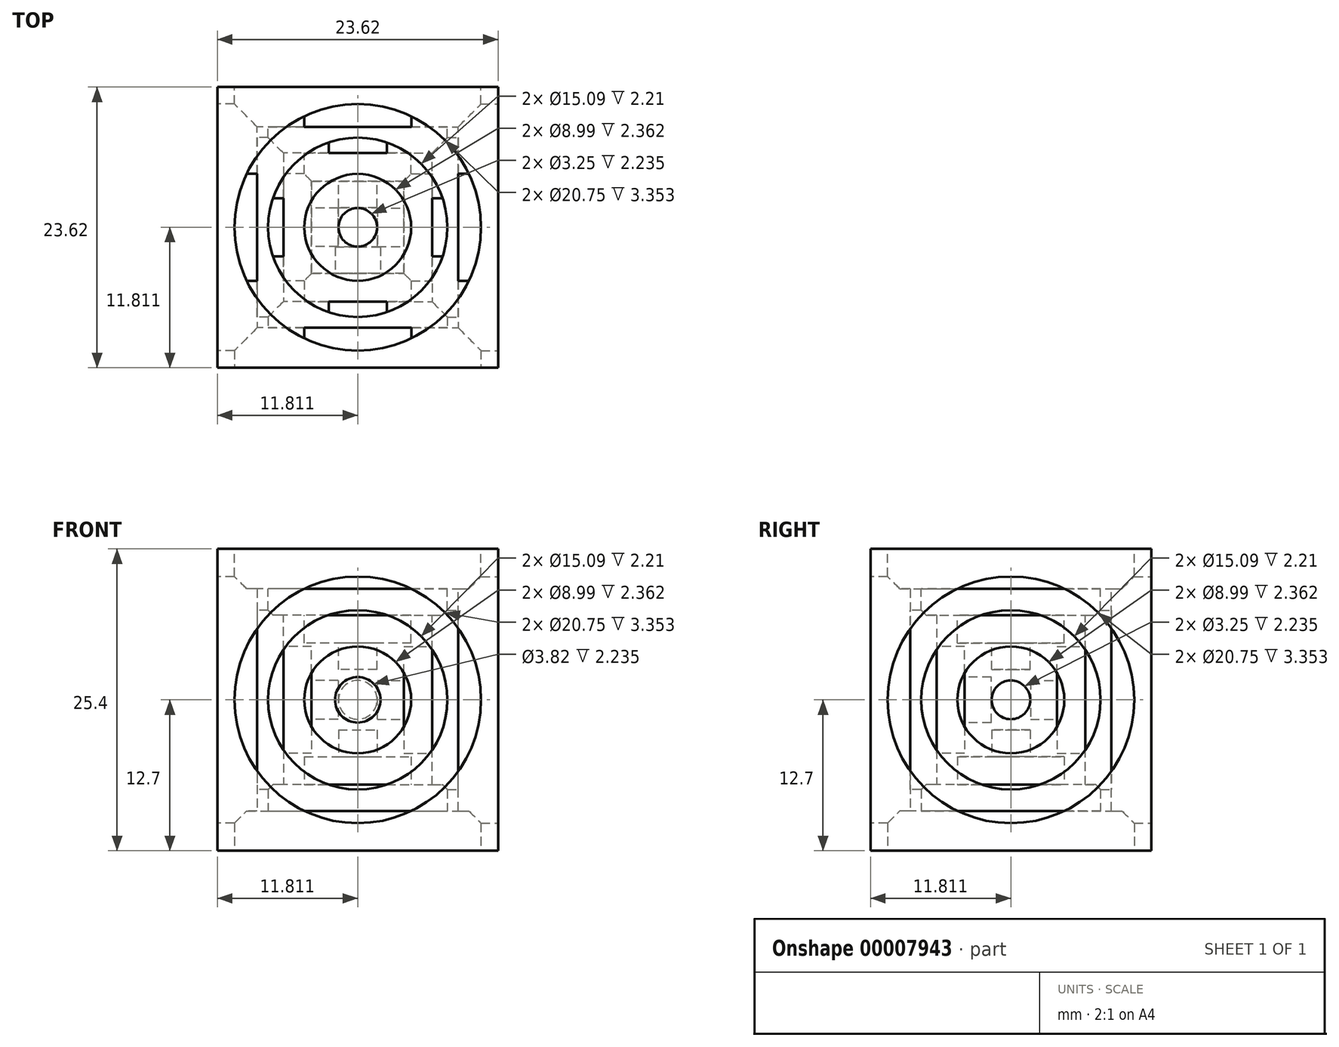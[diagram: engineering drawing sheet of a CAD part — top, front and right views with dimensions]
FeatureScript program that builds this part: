
annotation { "Feature Type Name" : "Feature", "Feature Type Description" : "" }
export const myFeature = defineFeature(function(context is Context, id is Id, definition is map)
    precondition{}
    {
        {
            var Q0;
            Q0=qCreatedBy(makeId("Top.planeOp"),FACE);
            var sketch = newSketch(context, id + "F0", { "sketchPlane" : qUnion([Q0])});
            skLineSegment(sketch, "E0.bottom", {"start": v(0, 0) * mm, "end": v(23.62, 0) * mm});
            skLineSegment(sketch, "E0.top", {"start": v(0, 23.62) * mm, "end": v(23.62, 23.62) * mm});
            skLineSegment(sketch, "E0.left", {"start": v(0, 0) * mm, "end": v(0, 23.62) * mm});
            skLineSegment(sketch, "E0.right", {"start": v(23.62, 0) * mm, "end": v(23.62, 23.62) * mm});
            skSolve(sketch);
        }
        {
            var Q0;
            Q0=makeQuery(id+"F0.imprint","IMPRINT",FACE,{"disambiguationData":[TD([[makeQuery(id+"F0.imprint","IMPRINT",EDGE,{"derivedFrom":sQuery(id+"F0.wireOp",EDGE,"E0.bottom")}),1.0]])]});
            extrude(context, id + "F1", {"entities" : qUnion([Q0]), "depth" : 25.4 * mm});
        }
        {
            var Q0;
            Q0=makeQuery(id+"F1.opExtrude","CAP_FACE",FACE,{"disambiguationData":[OSD([sQuery(id+"F0.wireOp",EDGE,"E0.bottom"),sQuery(id+"F0.wireOp",EDGE,"E0.top"),sQuery(id+"F0.wireOp",EDGE,"E0.left"),sQuery(id+"F0.wireOp",EDGE,"E0.right")])],"isStart":false});
            var sketch = newSketch(context, id + "F2", { "sketchPlane" : qUnion([Q0])});
            skCircle(sketch, "E1", {"center": v(11.81, 11.81) * mm, "radius": 1.63 * mm});
            skSolve(sketch);
        }
        {
            var Q0;
            Q0=makeQuery(id+"F2.imprint","IMPRINT",FACE,{"disambiguationData":[TD([[makeQuery(id+"F2.imprint","IMPRINT",EDGE,{"derivedFrom":sQuery(id+"F2.wireOp",EDGE,"E1")}),1.0]])]});
            extrude(context, id + "F3", {"entities" : qUnion([Q0]), "operationType" : NewBodyOperationType.REMOVE, "oppositeDirection" : true, "depth" : 10.16 * mm});
        }
        {
            var Q0;
            Q0=makeQuery(id+"F1.opExtrude","CAP_FACE",FACE,{"disambiguationData":[OSD([sQuery(id+"F0.wireOp",EDGE,"E0.bottom"),sQuery(id+"F0.wireOp",EDGE,"E0.top"),sQuery(id+"F0.wireOp",EDGE,"E0.left"),sQuery(id+"F0.wireOp",EDGE,"E0.right")])],"isStart":false});
            var sketch = newSketch(context, id + "F4", { "sketchPlane" : qUnion([Q0])});
            skCircle(sketch, "E2", {"center": v(11.81, 11.81) * mm, "radius": 4.5 * mm});
            skSolve(sketch);
        }
        {
            var Q0;
            Q0=makeQuery(id+"F4.imprint","IMPRINT",FACE,{"disambiguationData":[TD([[makeQuery(id+"F4.imprint","IMPRINT",EDGE,{"derivedFrom":sQuery(id+"F4.wireOp",EDGE,"E2")}),1.0]])]});
            extrude(context, id + "F5", {"entities" : qUnion([Q0]), "operationType" : NewBodyOperationType.REMOVE, "oppositeDirection" : true, "depth" : 7.92 * mm});
        }
        {
            var Q0;
            Q0=makeQuery(id+"F1.opExtrude","CAP_FACE",FACE,{"disambiguationData":[OSD([sQuery(id+"F0.wireOp",EDGE,"E0.bottom"),sQuery(id+"F0.wireOp",EDGE,"E0.top"),sQuery(id+"F0.wireOp",EDGE,"E0.left"),sQuery(id+"F0.wireOp",EDGE,"E0.right")])],"isStart":false});
            var sketch = newSketch(context, id + "F6", { "sketchPlane" : qUnion([Q0])});
            skCircle(sketch, "E3", {"center": v(11.81, 11.81) * mm, "radius": 7.54 * mm});
            skSolve(sketch);
        }
        {
            var Q0;
            Q0=makeQuery(id+"F6.imprint","IMPRINT",FACE,{"disambiguationData":[TD([[makeQuery(id+"F6.imprint","IMPRINT",EDGE,{"derivedFrom":sQuery(id+"F6.wireOp",EDGE,"E3")}),1.0]])]});
            extrude(context, id + "F7", {"entities" : qUnion([Q0]), "operationType" : NewBodyOperationType.REMOVE, "oppositeDirection" : true, "depth" : 5.56 * mm});
        }
        {
            var Q0;
            Q0=makeQuery(id+"F1.opExtrude","CAP_FACE",FACE,{"disambiguationData":[OSD([sQuery(id+"F0.wireOp",EDGE,"E0.bottom"),sQuery(id+"F0.wireOp",EDGE,"E0.top"),sQuery(id+"F0.wireOp",EDGE,"E0.left"),sQuery(id+"F0.wireOp",EDGE,"E0.right")])],"isStart":false});
            var sketch = newSketch(context, id + "F8", { "sketchPlane" : qUnion([Q0])});
            skCircle(sketch, "E4", {"center": v(11.81, 11.81) * mm, "radius": 10.38 * mm});
            skSolve(sketch);
        }
        {
            var Q0;
            Q0=makeQuery(id+"F8.imprint","IMPRINT",FACE,{"disambiguationData":[TD([[makeQuery(id+"F8.imprint","IMPRINT",EDGE,{"derivedFrom":sQuery(id+"F8.wireOp",EDGE,"E4")}),1.0]])]});
            extrude(context, id + "F9", {"entities" : qUnion([Q0]), "operationType" : NewBodyOperationType.REMOVE, "oppositeDirection" : true, "depth" : 3.35 * mm});
        }
        {
            var Q0;
            Q0=makeQuery(id+"F1.opExtrude","SWEPT_FACE",FACE,{"disambiguationData":[OSD([sQuery(id+"F0.wireOp",EDGE,"E0.bottom")])]});
            var sketch = newSketch(context, id + "F10", { "sketchPlane" : qUnion([Q0])});
            skCircle(sketch, "E5", {"center": v(11.81, 12.7) * mm, "radius": 1.91 * mm});
            skSolve(sketch);
        }
        {
            var Q0;
            Q0=makeQuery(id+"F10.imprint","IMPRINT",FACE,{"disambiguationData":[TD([[makeQuery(id+"F10.imprint","IMPRINT",EDGE,{"derivedFrom":sQuery(id+"F10.wireOp",EDGE,"E5")}),1.0]])]});
            extrude(context, id + "F11", {"entities" : qUnion([Q0]), "operationType" : NewBodyOperationType.REMOVE, "oppositeDirection" : true, "depth" : 10.16 * mm});
        }
        {
            var Q0;
            Q0=makeQuery(id+"F1.opExtrude","SWEPT_FACE",FACE,{"disambiguationData":[OSD([sQuery(id+"F0.wireOp",EDGE,"E0.bottom")])]});
            var sketch = newSketch(context, id + "F12", { "sketchPlane" : qUnion([Q0])});
            skCircle(sketch, "E6", {"center": v(11.81, 12.7) * mm, "radius": 4.5 * mm});
            skSolve(sketch);
        }
        {
            var Q0;
            Q0=makeQuery(id+"F12.imprint","IMPRINT",FACE,{"disambiguationData":[TD([[makeQuery(id+"F12.imprint","IMPRINT",EDGE,{"derivedFrom":sQuery(id+"F12.wireOp",EDGE,"E6")}),1.0]])]});
            extrude(context, id + "F13", {"entities" : qUnion([Q0]), "operationType" : NewBodyOperationType.REMOVE, "oppositeDirection" : true, "depth" : 7.92 * mm});
        }
        {
            var Q0;
            Q0=makeQuery(id+"F1.opExtrude","SWEPT_FACE",FACE,{"disambiguationData":[OSD([sQuery(id+"F0.wireOp",EDGE,"E0.bottom")])]});
            var sketch = newSketch(context, id + "F14", { "sketchPlane" : qUnion([Q0])});
            skCircle(sketch, "E7", {"center": v(11.81, 12.7) * mm, "radius": 7.54 * mm});
            skSolve(sketch);
        }
        {
            var Q0;
            Q0=makeQuery(id+"F14.imprint","IMPRINT",FACE,{"disambiguationData":[TD([[makeQuery(id+"F14.imprint","IMPRINT",EDGE,{"derivedFrom":sQuery(id+"F14.wireOp",EDGE,"E7")}),1.0]])]});
            extrude(context, id + "F15", {"entities" : qUnion([Q0]), "operationType" : NewBodyOperationType.REMOVE, "oppositeDirection" : true, "depth" : 5.56 * mm});
        }
        {
            var Q0;
            Q0=makeQuery(id+"F1.opExtrude","SWEPT_FACE",FACE,{"disambiguationData":[OSD([sQuery(id+"F0.wireOp",EDGE,"E0.bottom")])]});
            var sketch = newSketch(context, id + "F16", { "sketchPlane" : qUnion([Q0])});
            skCircle(sketch, "E8", {"center": v(11.81, 12.7) * mm, "radius": 10.38 * mm});
            skSolve(sketch);
        }
        {
            var Q0;
            Q0=makeQuery(id+"F16.imprint","IMPRINT",FACE,{"disambiguationData":[TD([[makeQuery(id+"F16.imprint","IMPRINT",EDGE,{"derivedFrom":sQuery(id+"F16.wireOp",EDGE,"E8")}),1.0]])]});
            extrude(context, id + "F17", {"entities" : qUnion([Q0]), "operationType" : NewBodyOperationType.REMOVE, "oppositeDirection" : true, "depth" : 3.35 * mm});
        }
        {
            var Q0;
            Q0=makeQuery(id+"F1.opExtrude","CAP_FACE",FACE,{"disambiguationData":[OSD([sQuery(id+"F0.wireOp",EDGE,"E0.bottom"),sQuery(id+"F0.wireOp",EDGE,"E0.top"),sQuery(id+"F0.wireOp",EDGE,"E0.left"),sQuery(id+"F0.wireOp",EDGE,"E0.right")])],"isStart":true});
            var sketch = newSketch(context, id + "F18", { "sketchPlane" : qUnion([Q0])});
            skCircle(sketch, "E9", {"center": v(11.81, -11.81) * mm, "radius": 1.63 * mm});
            skSolve(sketch);
        }
        {
            var Q0;
            Q0=makeQuery(id+"F18.imprint","IMPRINT",FACE,{"disambiguationData":[TD([[makeQuery(id+"F18.imprint","IMPRINT",EDGE,{"derivedFrom":sQuery(id+"F18.wireOp",EDGE,"E9")}),1.0]])]});
            extrude(context, id + "F19", {"entities" : qUnion([Q0]), "operationType" : NewBodyOperationType.REMOVE, "oppositeDirection" : true, "depth" : 10.16 * mm});
        }
        {
            var Q0;
            Q0=makeQuery(id+"F1.opExtrude","CAP_FACE",FACE,{"disambiguationData":[OSD([sQuery(id+"F0.wireOp",EDGE,"E0.bottom"),sQuery(id+"F0.wireOp",EDGE,"E0.top"),sQuery(id+"F0.wireOp",EDGE,"E0.left"),sQuery(id+"F0.wireOp",EDGE,"E0.right")])],"isStart":true});
            var sketch = newSketch(context, id + "F20", { "sketchPlane" : qUnion([Q0])});
            skCircle(sketch, "E10", {"center": v(11.81, -11.81) * mm, "radius": 4.5 * mm});
            skSolve(sketch);
        }
        {
            var Q0;
            Q0=makeQuery(id+"F20.imprint","IMPRINT",FACE,{"disambiguationData":[TD([[makeQuery(id+"F20.imprint","IMPRINT",EDGE,{"derivedFrom":sQuery(id+"F20.wireOp",EDGE,"E10")}),1.0]])]});
            extrude(context, id + "F21", {"entities" : qUnion([Q0]), "operationType" : NewBodyOperationType.REMOVE, "oppositeDirection" : true, "depth" : 7.92 * mm});
        }
        {
            var Q0;
            Q0=makeQuery(id+"F1.opExtrude","CAP_FACE",FACE,{"disambiguationData":[OSD([sQuery(id+"F0.wireOp",EDGE,"E0.bottom"),sQuery(id+"F0.wireOp",EDGE,"E0.top"),sQuery(id+"F0.wireOp",EDGE,"E0.left"),sQuery(id+"F0.wireOp",EDGE,"E0.right")])],"isStart":true});
            var sketch = newSketch(context, id + "F22", { "sketchPlane" : qUnion([Q0])});
            skCircle(sketch, "E11", {"center": v(11.81, -11.81) * mm, "radius": 7.54 * mm});
            skSolve(sketch);
        }
        {
            var Q0;
            Q0=makeQuery(id+"F22.imprint","IMPRINT",FACE,{"disambiguationData":[TD([[makeQuery(id+"F22.imprint","IMPRINT",EDGE,{"derivedFrom":sQuery(id+"F22.wireOp",EDGE,"E11")}),1.0]])]});
            extrude(context, id + "F23", {"entities" : qUnion([Q0]), "operationType" : NewBodyOperationType.REMOVE, "oppositeDirection" : true, "depth" : 5.56 * mm});
        }
        {
            var Q0;
            Q0=makeQuery(id+"F1.opExtrude","CAP_FACE",FACE,{"disambiguationData":[OSD([sQuery(id+"F0.wireOp",EDGE,"E0.bottom"),sQuery(id+"F0.wireOp",EDGE,"E0.top"),sQuery(id+"F0.wireOp",EDGE,"E0.left"),sQuery(id+"F0.wireOp",EDGE,"E0.right")])],"isStart":true});
            var sketch = newSketch(context, id + "F24", { "sketchPlane" : qUnion([Q0])});
            skCircle(sketch, "E12", {"center": v(11.81, -11.81) * mm, "radius": 10.38 * mm});
            skSolve(sketch);
        }
        {
            var Q0;
            Q0=makeQuery(id+"F24.imprint","IMPRINT",FACE,{"disambiguationData":[TD([[makeQuery(id+"F24.imprint","IMPRINT",EDGE,{"derivedFrom":sQuery(id+"F24.wireOp",EDGE,"E12")}),1.0]])]});
            extrude(context, id + "F25", {"entities" : qUnion([Q0]), "operationType" : NewBodyOperationType.REMOVE, "oppositeDirection" : true, "depth" : 3.35 * mm});
        }
        {
            var Q0;
            Q0=makeQuery(id+"F1.opExtrude","SWEPT_FACE",FACE,{"disambiguationData":[OSD([sQuery(id+"F0.wireOp",EDGE,"E0.right")])]});
            var sketch = newSketch(context, id + "F26", { "sketchPlane" : qUnion([Q0])});
            skCircle(sketch, "E13", {"center": v(11.81, 12.7) * mm, "radius": 1.63 * mm});
            skSolve(sketch);
        }
        {
            var Q0;
            Q0=makeQuery(id+"F26.imprint","IMPRINT",FACE,{"disambiguationData":[TD([[makeQuery(id+"F26.imprint","IMPRINT",EDGE,{"derivedFrom":sQuery(id+"F26.wireOp",EDGE,"E13")}),1.0]])]});
            extrude(context, id + "F27", {"entities" : qUnion([Q0]), "operationType" : NewBodyOperationType.REMOVE, "oppositeDirection" : true, "depth" : 10.16 * mm});
        }
        {
            var Q0;
            Q0=makeQuery(id+"F1.opExtrude","SWEPT_FACE",FACE,{"disambiguationData":[OSD([sQuery(id+"F0.wireOp",EDGE,"E0.right")])]});
            var sketch = newSketch(context, id + "F28", { "sketchPlane" : qUnion([Q0])});
            skCircle(sketch, "E14", {"center": v(11.81, 12.7) * mm, "radius": 4.5 * mm});
            skSolve(sketch);
        }
        {
            var Q0;
            Q0=makeQuery(id+"F28.imprint","IMPRINT",FACE,{"disambiguationData":[TD([[makeQuery(id+"F28.imprint","IMPRINT",EDGE,{"derivedFrom":sQuery(id+"F28.wireOp",EDGE,"E14")}),1.0]])]});
            extrude(context, id + "F29", {"entities" : qUnion([Q0]), "operationType" : NewBodyOperationType.REMOVE, "oppositeDirection" : true, "depth" : 7.92 * mm});
        }
        {
            var Q0;
            Q0=makeQuery(id+"F1.opExtrude","SWEPT_FACE",FACE,{"disambiguationData":[OSD([sQuery(id+"F0.wireOp",EDGE,"E0.right")])]});
            var sketch = newSketch(context, id + "F30", { "sketchPlane" : qUnion([Q0])});
            skCircle(sketch, "E15", {"center": v(11.81, 12.7) * mm, "radius": 7.54 * mm});
            skSolve(sketch);
        }
        {
            var Q0;
            Q0=makeQuery(id+"F30.imprint","IMPRINT",FACE,{"disambiguationData":[TD([[makeQuery(id+"F30.imprint","IMPRINT",EDGE,{"derivedFrom":sQuery(id+"F30.wireOp",EDGE,"E15")}),1.0]])]});
            extrude(context, id + "F31", {"entities" : qUnion([Q0]), "operationType" : NewBodyOperationType.REMOVE, "oppositeDirection" : true, "depth" : 5.56 * mm});
        }
        {
            var Q0;
            Q0=makeQuery(id+"F1.opExtrude","SWEPT_FACE",FACE,{"disambiguationData":[OSD([sQuery(id+"F0.wireOp",EDGE,"E0.right")])]});
            var sketch = newSketch(context, id + "F32", { "sketchPlane" : qUnion([Q0])});
            skCircle(sketch, "E16", {"center": v(11.81, 12.7) * mm, "radius": 10.38 * mm});
            skSolve(sketch);
        }
        {
            var Q0;
            Q0=makeQuery(id+"F32.imprint","IMPRINT",FACE,{"disambiguationData":[TD([[makeQuery(id+"F32.imprint","IMPRINT",EDGE,{"derivedFrom":sQuery(id+"F32.wireOp",EDGE,"E16")}),1.0]])]});
            extrude(context, id + "F33", {"entities" : qUnion([Q0]), "operationType" : NewBodyOperationType.REMOVE, "oppositeDirection" : true, "depth" : 3.35 * mm});
        }
        {
            var Q0;
            Q0=makeQuery(id+"F1.opExtrude","SWEPT_FACE",FACE,{"disambiguationData":[OSD([sQuery(id+"F0.wireOp",EDGE,"E0.top")])]});
            var sketch = newSketch(context, id + "F34", { "sketchPlane" : qUnion([Q0])});
            skCircle(sketch, "E17", {"center": v(-11.81, 12.7) * mm, "radius": 1.63 * mm});
            skSolve(sketch);
        }
        {
            var Q0;
            Q0=makeQuery(id+"F34.imprint","IMPRINT",FACE,{"disambiguationData":[TD([[makeQuery(id+"F34.imprint","IMPRINT",EDGE,{"derivedFrom":sQuery(id+"F34.wireOp",EDGE,"E17")}),1.0]])]});
            extrude(context, id + "F35", {"entities" : qUnion([Q0]), "operationType" : NewBodyOperationType.REMOVE, "oppositeDirection" : true, "depth" : 10.16 * mm});
        }
        {
            var Q0;
            Q0=makeQuery(id+"F1.opExtrude","SWEPT_FACE",FACE,{"disambiguationData":[OSD([sQuery(id+"F0.wireOp",EDGE,"E0.top")])]});
            var sketch = newSketch(context, id + "F36", { "sketchPlane" : qUnion([Q0])});
            skCircle(sketch, "E18", {"center": v(-11.81, 12.7) * mm, "radius": 4.5 * mm});
            skSolve(sketch);
        }
        {
            var Q0;
            Q0=makeQuery(id+"F36.imprint","IMPRINT",FACE,{"disambiguationData":[TD([[makeQuery(id+"F36.imprint","IMPRINT",EDGE,{"derivedFrom":sQuery(id+"F36.wireOp",EDGE,"E18")}),1.0]])]});
            extrude(context, id + "F37", {"entities" : qUnion([Q0]), "operationType" : NewBodyOperationType.REMOVE, "oppositeDirection" : true, "depth" : 7.92 * mm});
        }
        {
            var Q0;
            Q0=makeQuery(id+"F1.opExtrude","SWEPT_FACE",FACE,{"disambiguationData":[OSD([sQuery(id+"F0.wireOp",EDGE,"E0.top")])]});
            var sketch = newSketch(context, id + "F38", { "sketchPlane" : qUnion([Q0])});
            skCircle(sketch, "E19", {"center": v(-11.81, 12.7) * mm, "radius": 7.54 * mm});
            skSolve(sketch);
        }
        {
            var Q0;
            Q0=makeQuery(id+"F38.imprint","IMPRINT",FACE,{"disambiguationData":[TD([[makeQuery(id+"F38.imprint","IMPRINT",EDGE,{"derivedFrom":sQuery(id+"F38.wireOp",EDGE,"E19")}),1.0]])]});
            extrude(context, id + "F39", {"entities" : qUnion([Q0]), "operationType" : NewBodyOperationType.REMOVE, "oppositeDirection" : true, "depth" : 5.56 * mm});
        }
        {
            var Q0;
            Q0=makeQuery(id+"F1.opExtrude","SWEPT_FACE",FACE,{"disambiguationData":[OSD([sQuery(id+"F0.wireOp",EDGE,"E0.top")])]});
            var sketch = newSketch(context, id + "F40", { "sketchPlane" : qUnion([Q0])});
            skCircle(sketch, "E20", {"center": v(-11.81, 12.7) * mm, "radius": 10.38 * mm});
            skSolve(sketch);
        }
        {
            var Q0;
            Q0=makeQuery(id+"F40.imprint","IMPRINT",FACE,{"disambiguationData":[TD([[makeQuery(id+"F40.imprint","IMPRINT",EDGE,{"derivedFrom":sQuery(id+"F40.wireOp",EDGE,"E20")}),1.0]])]});
            extrude(context, id + "F41", {"entities" : qUnion([Q0]), "operationType" : NewBodyOperationType.REMOVE, "oppositeDirection" : true, "depth" : 3.35 * mm});
        }
        {
            var Q0;
            Q0=makeQuery(id+"F1.opExtrude","SWEPT_FACE",FACE,{"disambiguationData":[OSD([sQuery(id+"F0.wireOp",EDGE,"E0.left")])]});
            var sketch = newSketch(context, id + "F42", { "sketchPlane" : qUnion([Q0])});
            skCircle(sketch, "E21", {"center": v(-11.81, 12.7) * mm, "radius": 1.63 * mm});
            skSolve(sketch);
        }
        {
            var Q0;
            Q0=makeQuery(id+"F42.imprint","IMPRINT",FACE,{"disambiguationData":[TD([[makeQuery(id+"F42.imprint","IMPRINT",EDGE,{"derivedFrom":sQuery(id+"F42.wireOp",EDGE,"E21")}),1.0]])]});
            extrude(context, id + "F43", {"entities" : qUnion([Q0]), "operationType" : NewBodyOperationType.REMOVE, "oppositeDirection" : true, "depth" : 10.16 * mm});
        }
        {
            var Q0;
            Q0=makeQuery(id+"F1.opExtrude","SWEPT_FACE",FACE,{"disambiguationData":[OSD([sQuery(id+"F0.wireOp",EDGE,"E0.left")])]});
            var sketch = newSketch(context, id + "F44", { "sketchPlane" : qUnion([Q0])});
            skCircle(sketch, "E22", {"center": v(-11.81, 12.7) * mm, "radius": 4.5 * mm});
            skSolve(sketch);
        }
        {
            var Q0;
            Q0=makeQuery(id+"F44.imprint","IMPRINT",FACE,{"disambiguationData":[TD([[makeQuery(id+"F44.imprint","IMPRINT",EDGE,{"derivedFrom":sQuery(id+"F44.wireOp",EDGE,"E22")}),1.0]])]});
            extrude(context, id + "F45", {"entities" : qUnion([Q0]), "operationType" : NewBodyOperationType.REMOVE, "oppositeDirection" : true, "depth" : 7.92 * mm});
        }
        {
            var Q0;
            Q0=makeQuery(id+"F1.opExtrude","SWEPT_FACE",FACE,{"disambiguationData":[OSD([sQuery(id+"F0.wireOp",EDGE,"E0.left")])]});
            var sketch = newSketch(context, id + "F46", { "sketchPlane" : qUnion([Q0])});
            skCircle(sketch, "E23", {"center": v(-11.81, 12.7) * mm, "radius": 7.54 * mm});
            skSolve(sketch);
        }
        {
            var Q0;
            Q0=makeQuery(id+"F46.imprint","IMPRINT",FACE,{"disambiguationData":[TD([[makeQuery(id+"F46.imprint","IMPRINT",EDGE,{"derivedFrom":sQuery(id+"F46.wireOp",EDGE,"E23")}),1.0]])]});
            extrude(context, id + "F47", {"entities" : qUnion([Q0]), "operationType" : NewBodyOperationType.REMOVE, "oppositeDirection" : true, "depth" : 5.56 * mm});
        }
        {
            var Q0;
            Q0=makeQuery(id+"F1.opExtrude","SWEPT_FACE",FACE,{"disambiguationData":[OSD([sQuery(id+"F0.wireOp",EDGE,"E0.left")])]});
            var sketch = newSketch(context, id + "F48", { "sketchPlane" : qUnion([Q0])});
            skCircle(sketch, "E24", {"center": v(-11.81, 12.7) * mm, "radius": 10.38 * mm});
            skSolve(sketch);
        }
        {
            var Q0;
            Q0=makeQuery(id+"F48.imprint","IMPRINT",FACE,{"disambiguationData":[TD([[makeQuery(id+"F48.imprint","IMPRINT",EDGE,{"derivedFrom":sQuery(id+"F48.wireOp",EDGE,"E24")}),1.0]])]});
            extrude(context, id + "F49", {"entities" : qUnion([Q0]), "operationType" : NewBodyOperationType.REMOVE, "oppositeDirection" : true, "depth" : 3.35 * mm});
        }
    });
